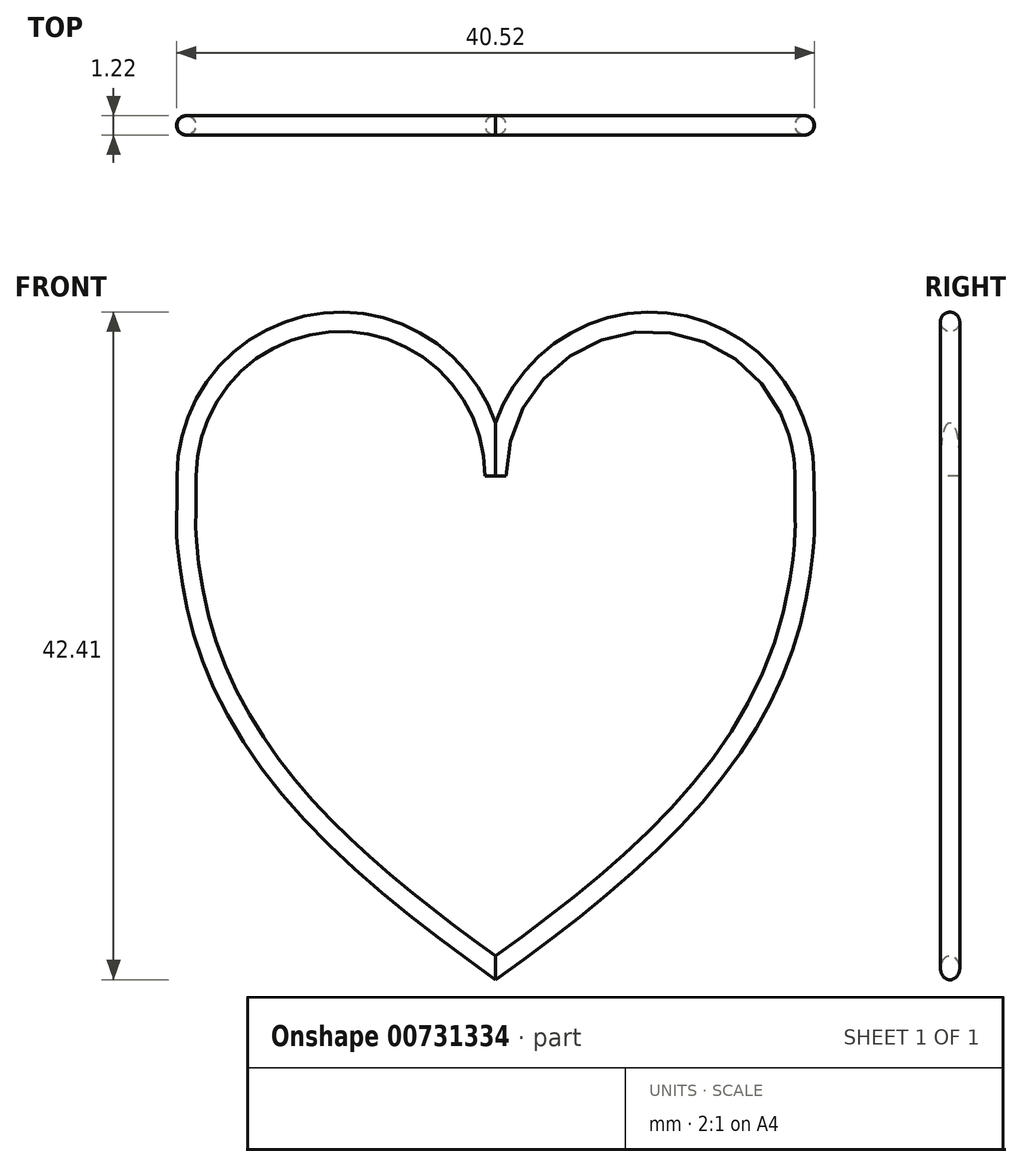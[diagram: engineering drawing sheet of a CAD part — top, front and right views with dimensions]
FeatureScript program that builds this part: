
annotation { "Feature Type Name" : "Feature", "Feature Type Description" : "" }
export const myFeature = defineFeature(function(context is Context, id is Id, definition is map)
    precondition{}
    {
        {
            var Q0;
            Q0=qCreatedBy(makeId("Front.planeOp"),FACE);
            var sketch = newSketch(context, id + "F0", { "sketchPlane" : qUnion([Q0])});
            skArc(sketch, "E0", {"start": v(19.68, 0) * mm, "mid": v(9.84, 9.84) * mm, "end": v(0, 0) * mm});
            skFitSpline(sketch, "E1", {"points": [v(19.68, 0) * mm, v(19.68, -4) * mm, v(18.57, -10.16) * mm, v(12.58, -20.54) * mm, v(0, -31.32) * mm], "startDerivative": vector(0, -58.9) * mm, "endDerivative": vector(-41.32, -29.7) * mm});
            skArc(sketch, "E2.MirrorCS", {"start": v(-19.68, 0) * mm, "mid": v(-9.84, 9.84) * mm, "end": v(0, 0) * mm});
            skFitSpline(sketch, "E3.MirrorCS", {"points": [v(-19.68, 0) * mm, v(-19.68, -4) * mm, v(-18.57, -10.16) * mm, v(-12.58, -20.54) * mm, v(0, -31.32) * mm], "startDerivative": vector(0, -58.9) * mm, "endDerivative": vector(41.32, -29.7) * mm});
            skSolve(sketch);
        }
        {
            var Q0;
            Q0=qCreatedBy(makeId("Top.planeOp"),FACE);
            var sketch = newSketch(context, id + "F1", { "sketchPlane" : qUnion([Q0])});
            skCircle(sketch, "E4", {"center": v(19.62, 0) * mm, "radius": 0.61 * mm});
            skSolve(sketch);
        }
        {
            var Q0;
            Q0=makeQuery(id+"F1.imprint","IMPRINT",FACE,{"disambiguationData":[TD([[makeQuery(id+"F1.imprint","IMPRINT",EDGE,{"derivedFrom":sQuery(id+"F1.wireOp",EDGE,"E4")}),1.0]])]});
            var Q1;
            Q1=sQuery(id+"F0.wireOp",EDGE,"E1");
            var Q2;
            Q2=sQuery(id+"F0.wireOp",EDGE,"E3.MirrorCS");
            var Q3;
            Q3=sQuery(id+"F0.wireOp",EDGE,"E2.MirrorCS");
            sweep(context, id + "F2", {"profiles" : qUnion([Q0]), "path" : qUnion([Q1, Q2, Q3])});
        }
        {
            var Q0;
            Q0=makeQuery(id+"F1.imprint","IMPRINT",FACE,{"disambiguationData":[TD([[makeQuery(id+"F1.imprint","IMPRINT",EDGE,{"derivedFrom":sQuery(id+"F1.wireOp",EDGE,"E4")}),1.0]])]});
            var Q1;
            Q1=sQuery(id+"F0.wireOp",EDGE,"E0");
            sweep(context, id + "F3", {"operationType" : NewBodyOperationType.ADD, "profiles" : qUnion([Q0]), "path" : qUnion([Q1])});
        }
    });
